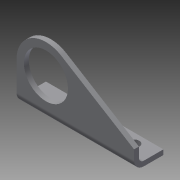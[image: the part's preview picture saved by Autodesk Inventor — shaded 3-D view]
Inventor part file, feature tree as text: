
AUTODESK INVENTOR PART (.ipt)
format: ipt  version: 2013 (Build 170138000, 138)  size: 133,632 bytes
history: native  units: in
note: dims shown in document units (in); Inventor stores cm internally (conversion verified against a paired STEP export)
features: sheet_metal_op x4, sketch x4, other x4
ambient origin geometry x8: Origin, YZ Plane, XZ Plane, XY Plane, X Axis, Y Axis, Z Axis, Center Point
feature tree (12):
  sheet_metal_op  "Face2"
  sheet_metal_op  "Flange1"
  sketch  "Sketch1"  dims[d0=0.5in]
  other  "Plate2"
  sketch  "Sketch2"  dims[d2=3.0in]
  other  "Plate3"
  sheet_metal_op  "Bend1"
  sheet_metal_op  "Corner1"
  sketch  "Sketch3"  dims[d5=0.266in]
  sketch  "Sketch4"  dims[d7=0.266in d8=0.25in d9=1.5in d10=0.25in d11=0.5in d12=1.5in d18=0.125in d19=0.125in d20=0.125in d21=0.0625in d22=0.25in d23=0.125in d24=1.75in d25=90.0deg d26=0.125in d27=0.5in d28=0.125in d29=0.125in d30=1.125in d31=0.75in d32=0.75in d33=0.125in d34=0.0in d35=0.25in d36=0.125in d37=0.0in]
  other  "Cut1"
  other  "Cut2"
